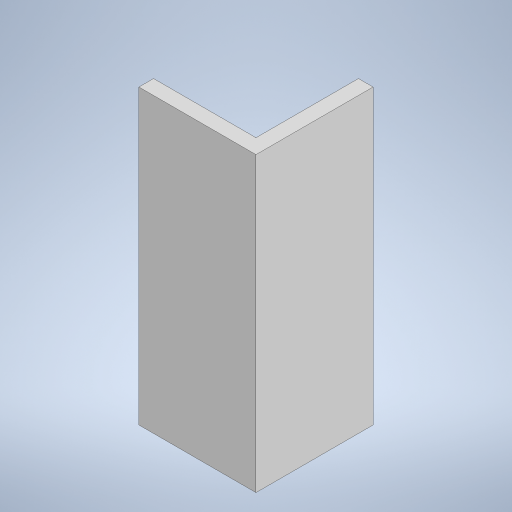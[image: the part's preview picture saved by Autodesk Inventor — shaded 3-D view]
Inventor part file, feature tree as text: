
AUTODESK INVENTOR PART (.ipt)
format: ipt  version: 2023 (Build 270158000, 158)  size: 222,208 bytes
history: native  units: in
note: dims shown in document units (in); Inventor stores cm internally (conversion verified against a paired STEP export)
features: extrude x1, sketch x1
ambient origin geometry x8: Origin, YZ Plane, XZ Plane, XY Plane, X Axis, Y Axis, Z Axis, Center Point
bodies: Solid1 (feature_tree)
feature tree (2):
  extrude  "Extrusion1"  Depth=0.125in
  sketch  "Sketch1"  dims[d0=1.0in d1=0.125in d2=0.875in d3=0.875in d4=2.5in d5=0.0in]
